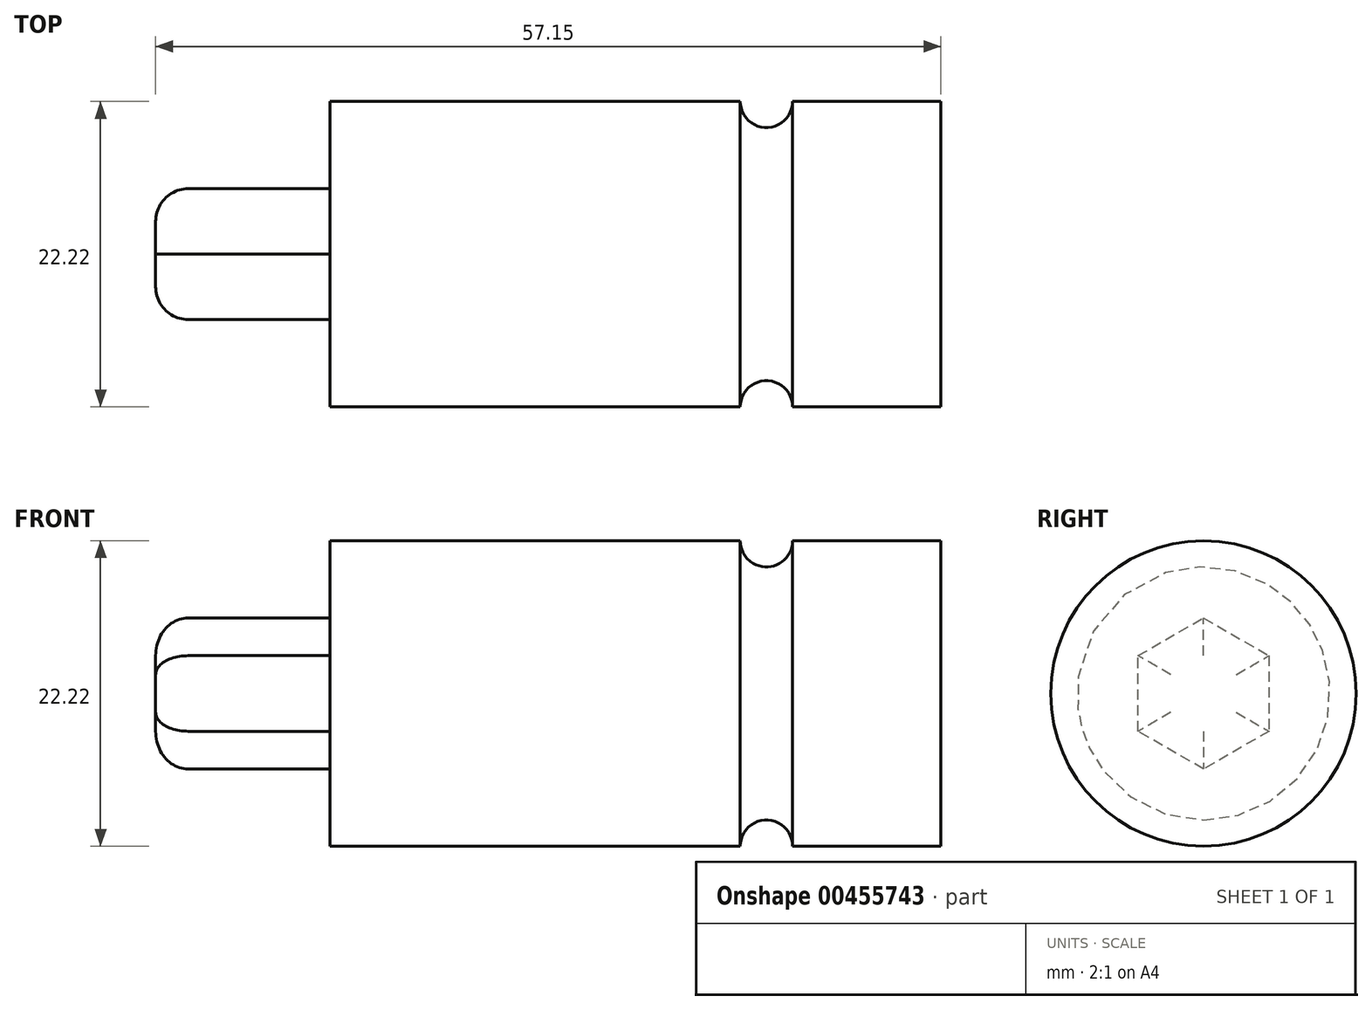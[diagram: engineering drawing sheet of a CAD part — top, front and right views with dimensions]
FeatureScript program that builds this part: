
annotation { "Feature Type Name" : "Feature", "Feature Type Description" : "" }
export const myFeature = defineFeature(function(context is Context, id is Id, definition is map)
    precondition{}
    {
        {
            var Q0;
            Q0=qCreatedBy(makeId("Right.planeOp"),FACE);
            var sketch = newSketch(context, id + "F0", { "sketchPlane" : qUnion([Q0])});
            skCircle(sketch, "E0", {"center": v(0, 0) * mm, "radius": 11.11 * mm});
            skSolve(sketch);
        }
        {
            var Q0;
            Q0 = qSketchRegion(id + "F0", true);
            extrude(context, id + "F1", {"entities" : qUnion([Q0]), "depth" : 44.45 * mm});
        }
        {
            var Q0;
            Q0=qCreatedBy(makeId("Right.planeOp"),FACE);
            var sketch = newSketch(context, id + "F2", { "sketchPlane" : qUnion([Q0])});
            skCircle(sketch, "E1.cCircle", {"center": v(0, 0) * mm, "radius": 4.76 * mm, "construction": true});
            skLineSegment(sketch, "E1.0", {"start": v(-4.76, -2.75) * mm, "end": v(-4.76, 2.75) * mm});
            skLineSegment(sketch, "E1.1", {"start": v(-4.76, 2.75) * mm, "end": v(0, 5.5) * mm});
            skLineSegment(sketch, "E1.2", {"start": v(0, 5.5) * mm, "end": v(4.76, 2.75) * mm});
            skLineSegment(sketch, "E1.3", {"start": v(4.76, 2.75) * mm, "end": v(4.76, -2.75) * mm});
            skLineSegment(sketch, "E1.4", {"start": v(4.76, -2.75) * mm, "end": v(0, -5.5) * mm});
            skLineSegment(sketch, "E1.5", {"start": v(0, -5.5) * mm, "end": v(-4.76, -2.75) * mm});
            skPoint(sketch, "E1.0.midPoint", {"position": v(-4.76, 0) * mm});
            skSolve(sketch);
        }
        {
            var Q0;
            Q0 = qSketchRegion(id + "F2", true);
            extrude(context, id + "F3", {"entities" : qUnion([Q0]), "operationType" : NewBodyOperationType.ADD, "oppositeDirection" : true, "depth" : 12.7 * mm, "offsetDistance" : 25.4 * mm});
        }
        {
            var Q0;
            Q0=makeQuery(id+"F3.opExtrude","CAP_EDGE",EDGE,{"disambiguationData":[OSD([sQuery(id+"F2.wireOp",EDGE,"E1.1")])],"isStart":false});
            var Q1;
            Q1=makeQuery(id+"F3.opExtrude","CAP_EDGE",EDGE,{"disambiguationData":[OSD([sQuery(id+"F2.wireOp",EDGE,"E1.2")])],"isStart":false});
            var Q2;
            Q2=makeQuery(id+"F3.opExtrude","CAP_EDGE",EDGE,{"disambiguationData":[OSD([sQuery(id+"F2.wireOp",EDGE,"E1.3")])],"isStart":false});
            var Q3;
            Q3=makeQuery(id+"F3.opExtrude","CAP_EDGE",EDGE,{"disambiguationData":[OSD([sQuery(id+"F2.wireOp",EDGE,"E1.4")])],"isStart":false});
            var Q4;
            Q4=makeQuery(id+"F3.opExtrude","CAP_EDGE",EDGE,{"disambiguationData":[OSD([sQuery(id+"F2.wireOp",EDGE,"E1.5")])],"isStart":false});
            var Q5;
            Q5=makeQuery(id+"F3.opExtrude","CAP_EDGE",EDGE,{"disambiguationData":[OSD([sQuery(id+"F2.wireOp",EDGE,"E1.0")])],"isStart":false});
            fillet(context, id + "F4", {"entities" : qUnion([Q0, Q1, Q2, Q3, Q4, Q5]), "radius" : 2.38 * mm, "tangentPropagation" : true, "allowEdgeOverflow" : false});
        }
        {
            var Q0;
            Q0=makeQuery(id+"F1.opExtrude","CAP_FACE",FACE,{"disambiguationData":[OSD([sQuery(id+"F0.wireOp",EDGE,"E0")])],"isStart":false});
            var sketch = newSketch(context, id + "F5", { "sketchPlane" : qUnion([Q0])});
            skPoint(sketch, "E2", {"position": v(0, 0) * mm});
            skSolve(sketch);
        }
        {
            var Q0;
            Q0=qCreatedBy(makeId("Front.planeOp"),FACE);
            var sketch = newSketch(context, id + "F6", { "sketchPlane" : qUnion([Q0])});
            skCircle(sketch, "E3", {"center": v(31.75, 11.11) * mm, "radius": 1.9 * mm});
            skLineSegment(sketch, "E4", {"start": v(0, 0) * mm, "end": v(79.53, 0) * mm, "construction": true});
            skSolve(sketch);
        }
        {
            var Q0;
            Q0=makeQuery(id+"F6.imprint","IMPRINT",FACE,{"disambiguationData":[TD([[makeQuery(id+"F6.imprint","IMPRINT",EDGE,{"derivedFrom":sQuery(id+"F6.wireOp",EDGE,"E3")}),1.0]])]});
            var Q1;
            Q1=sQuery(id+"F6.wireOp",EDGE,"E3");
            var Q2;
            Q2=sQuery(id+"F6.wireOp",EDGE,"E4");
            revolve(context, id + "F7", {"operationType" : NewBodyOperationType.REMOVE, "entities" : qUnion([Q0]), "surfaceEntities" : qUnion([Q1]), "axis" : qUnion([Q2]), "revolveType" : RevolveType.FULL, "oppositeDirection" : true});
        }
    });
